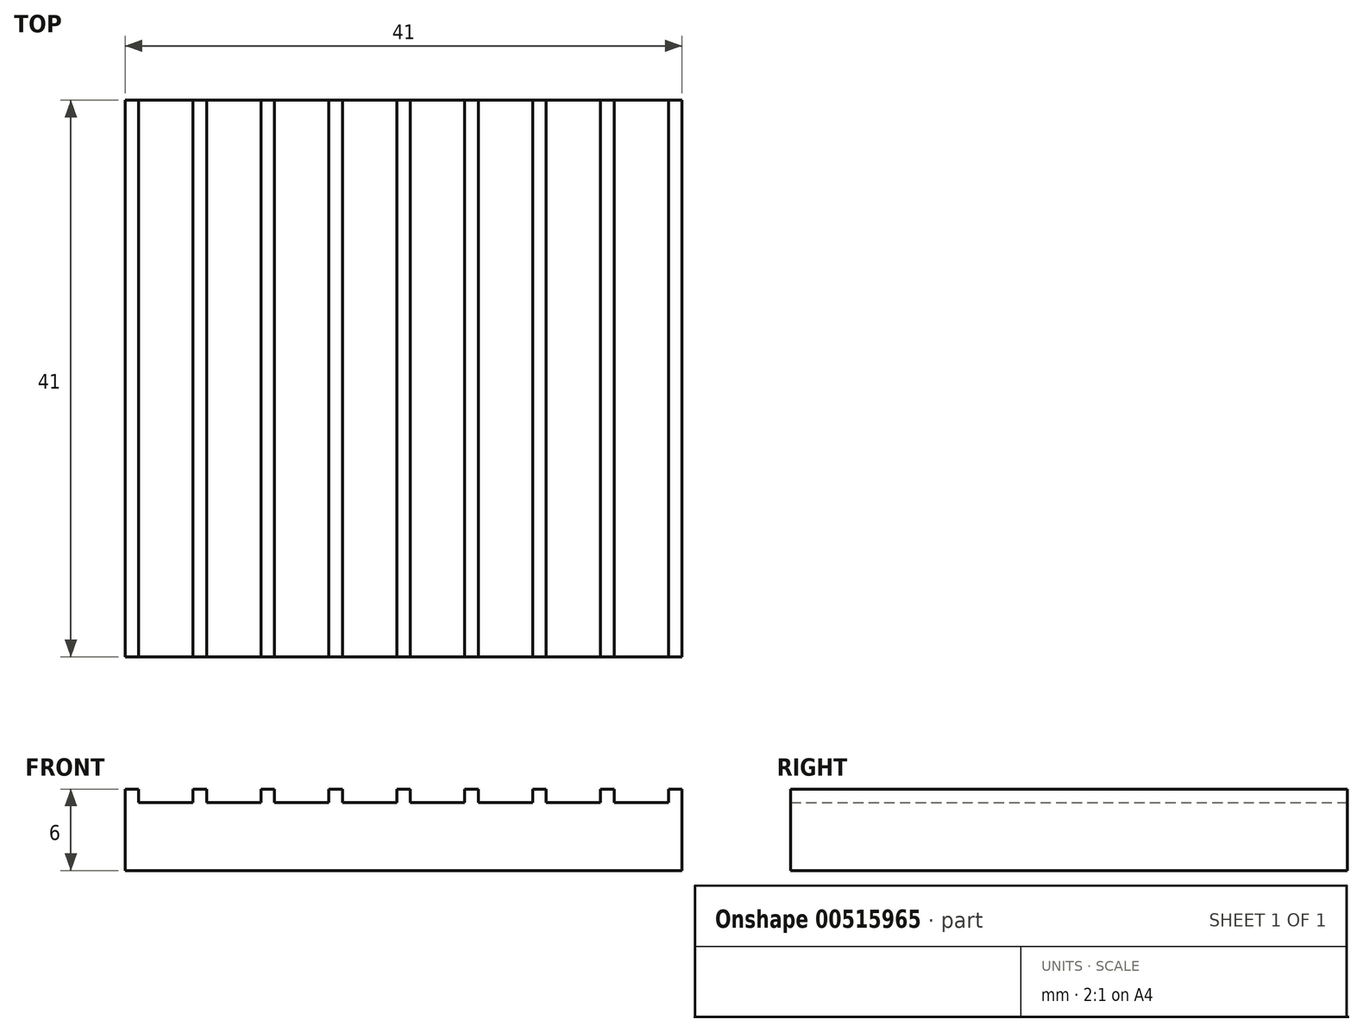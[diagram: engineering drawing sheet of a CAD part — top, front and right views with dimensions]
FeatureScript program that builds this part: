
annotation { "Feature Type Name" : "Feature", "Feature Type Description" : "" }
export const myFeature = defineFeature(function(context is Context, id is Id, definition is map)
    precondition{}
    {
        {
            var Q0;
            Q0=qCreatedBy(makeId("Front.planeOp"),FACE);
            var sketch = newSketch(context, id + "F0", { "sketchPlane" : qUnion([Q0])});
            skLineSegment(sketch, "E0", {"start": v(0, 0) * mm, "end": v(41, 0) * mm});
            skLineSegment(sketch, "E1", {"start": v(41, 0) * mm, "end": v(41, 6) * mm});
            skLineSegment(sketch, "E2", {"start": v(41, 6) * mm, "end": v(40, 6) * mm});
            skLineSegment(sketch, "E3", {"start": v(40, 6) * mm, "end": v(40, 5) * mm});
            skLineSegment(sketch, "E4", {"start": v(40, 5) * mm, "end": v(36, 5) * mm});
            skLineSegment(sketch, "E5", {"start": v(36, 5) * mm, "end": v(36, 6) * mm});
            skLineSegment(sketch, "E6", {"start": v(36, 6) * mm, "end": v(35, 6) * mm});
            skLineSegment(sketch, "E7", {"start": v(35, 6) * mm, "end": v(35, 5) * mm});
            skLineSegment(sketch, "E8", {"start": v(35, 5) * mm, "end": v(31, 5) * mm});
            skLineSegment(sketch, "E9", {"start": v(31, 5) * mm, "end": v(31, 6) * mm});
            skLineSegment(sketch, "E10", {"start": v(31, 6) * mm, "end": v(30, 6) * mm});
            skLineSegment(sketch, "E11", {"start": v(30, 6) * mm, "end": v(30, 5) * mm});
            skLineSegment(sketch, "E12", {"start": v(30, 5) * mm, "end": v(26, 5) * mm});
            skLineSegment(sketch, "E13", {"start": v(26, 5) * mm, "end": v(26, 6) * mm});
            skLineSegment(sketch, "E14", {"start": v(26, 6) * mm, "end": v(25, 6) * mm});
            skLineSegment(sketch, "E15", {"start": v(25, 6) * mm, "end": v(25, 5) * mm});
            skLineSegment(sketch, "E16", {"start": v(25, 5) * mm, "end": v(21, 5) * mm});
            skLineSegment(sketch, "E17", {"start": v(21, 5) * mm, "end": v(21, 6) * mm});
            skLineSegment(sketch, "E18", {"start": v(21, 6) * mm, "end": v(20, 6) * mm});
            skLineSegment(sketch, "E19", {"start": v(20, 6) * mm, "end": v(20, 5) * mm});
            skLineSegment(sketch, "E20", {"start": v(20, 5) * mm, "end": v(16, 5) * mm});
            skLineSegment(sketch, "E21", {"start": v(16, 5) * mm, "end": v(16, 6) * mm});
            skLineSegment(sketch, "E22", {"start": v(16, 6) * mm, "end": v(15, 6) * mm});
            skLineSegment(sketch, "E23", {"start": v(15, 6) * mm, "end": v(15, 5) * mm});
            skLineSegment(sketch, "E24", {"start": v(15, 5) * mm, "end": v(11, 5) * mm});
            skLineSegment(sketch, "E25", {"start": v(11, 5) * mm, "end": v(11, 6) * mm});
            skLineSegment(sketch, "E26", {"start": v(11, 6) * mm, "end": v(10, 6) * mm});
            skLineSegment(sketch, "E27", {"start": v(10, 6) * mm, "end": v(10, 5) * mm});
            skLineSegment(sketch, "E28", {"start": v(10, 5) * mm, "end": v(6, 5) * mm});
            skLineSegment(sketch, "E29", {"start": v(6, 5) * mm, "end": v(6, 6) * mm});
            skLineSegment(sketch, "E30", {"start": v(6, 6) * mm, "end": v(5, 6) * mm});
            skLineSegment(sketch, "E31", {"start": v(5, 6) * mm, "end": v(5, 5) * mm});
            skLineSegment(sketch, "E32", {"start": v(5, 5) * mm, "end": v(1, 5) * mm});
            skLineSegment(sketch, "E33", {"start": v(1, 5) * mm, "end": v(1, 6) * mm});
            skLineSegment(sketch, "E34", {"start": v(1, 6) * mm, "end": v(0, 6) * mm});
            skLineSegment(sketch, "E35", {"start": v(0, 6) * mm, "end": v(0, 0) * mm});
            skSolve(sketch);
        }
        {
            var Q0;
            Q0 = qSketchRegion(id + "F0", true);
            extrude(context, id + "F1", {"entities" : qUnion([Q0]), "depth" : 41 * mm, "offsetDistance" : 25 * mm});
        }
    });
